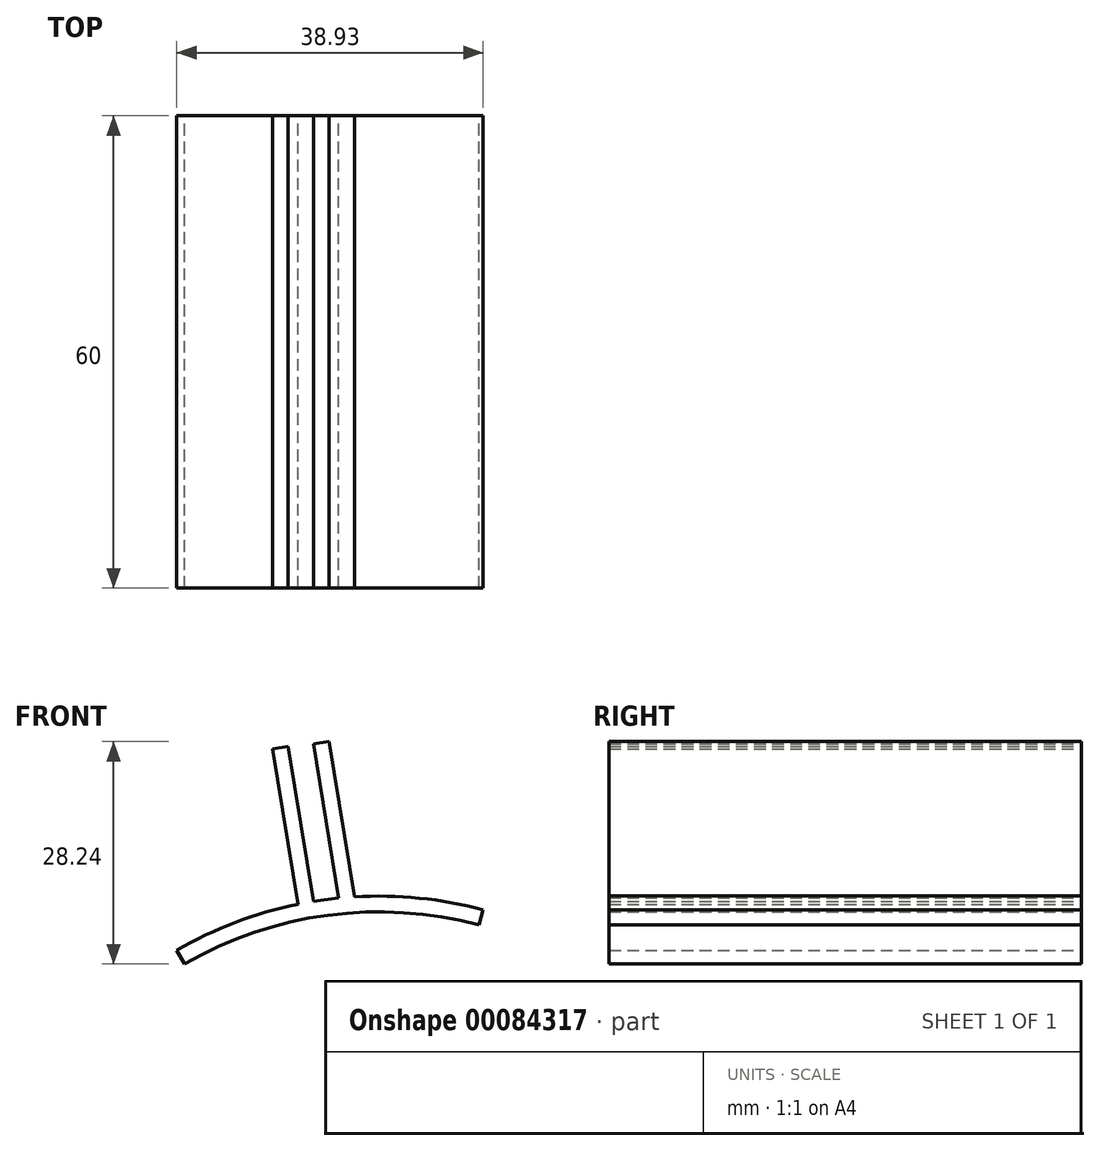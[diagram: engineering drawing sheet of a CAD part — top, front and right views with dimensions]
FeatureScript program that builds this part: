
annotation { "Feature Type Name" : "Feature", "Feature Type Description" : "" }
export const myFeature = defineFeature(function(context is Context, id is Id, definition is map)
    precondition{}
    {
        {
            var Q0;
            Q0=qCreatedBy(makeId("Front.planeOp"),FACE);
            var sketch = newSketch(context, id + "F0", { "sketchPlane" : qUnion([Q0])});
            skCircle(sketch, "E0", {"center": v(0, 0) * mm, "radius": 49.3 * mm});
            skLineSegment(sketch, "E1", {"start": v(0, 0) * mm, "end": v(-24.65, 42.7) * mm});
            skLineSegment(sketch, "E2", {"start": v(0, 0) * mm, "end": v(49.3, 0) * mm});
            skLineSegment(sketch, "E3", {"start": v(0, 0) * mm, "end": v(-24.65, -42.7) * mm});
            skArc(sketch, "E4", {"start": v(-24.65, 42.7) * mm, "mid": v(-6.43, 48.88) * mm, "end": v(12.76, 47.62) * mm});
            skLineSegment(sketch, "E5", {"start": v(0, 0) * mm, "end": v(12.76, 47.62) * mm});
            skArc(sketch, "E6", {"start": v(-24.65, -42.7) * mm, "mid": v(-14.82, -47.02) * mm, "end": v(-4.3, -49.11) * mm});
            skLineSegment(sketch, "E7", {"start": v(0, 0) * mm, "end": v(-4.3, -49.11) * mm});
            skArc(sketch, "E8", {"start": v(49.3, 0) * mm, "mid": v(48.13, 10.67) * mm, "end": v(44.68, 20.84) * mm});
            skLineSegment(sketch, "E9", {"start": v(0, 0) * mm, "end": v(44.68, 20.84) * mm});
            skCircle(sketch, "E10", {"center": v(0, 0) * mm, "radius": 51.3 * mm});
            skLineSegment(sketch, "E11", {"start": v(12.76, 47.62) * mm, "end": v(13.28, 49.55) * mm});
            skLineSegment(sketch, "E12", {"start": v(-24.65, 42.7) * mm, "end": v(-25.65, 44.43) * mm});
            skLineSegment(sketch, "E13", {"start": v(-24.65, -42.7) * mm, "end": v(-31.2, -40.72) * mm});
            skLineSegment(sketch, "E14", {"start": v(-8.3, 50.62) * mm, "end": v(-11.53, 70.32) * mm});
            skLineSegment(sketch, "E15", {"start": v(-5.09, 51.05) * mm, "end": v(-8.3, 70.62) * mm});
            skLineSegment(sketch, "E16", {"start": v(-8.3, 70.62) * mm, "end": v(-6.32, 70.94) * mm});
            skLineSegment(sketch, "E17", {"start": v(-6.32, 70.94) * mm, "end": v(-3.09, 51.2) * mm});
            skLineSegment(sketch, "E18", {"start": v(-11.53, 70.32) * mm, "end": v(-13.5, 70) * mm});
            skLineSegment(sketch, "E19", {"start": v(-13.5, 70) * mm, "end": v(-10.27, 50.26) * mm});
            skLineSegment(sketch, "E20", {"start": v(-11.53, 70.32) * mm, "end": v(-8.3, 70.62) * mm});
            skLineSegment(sketch, "E21", {"start": v(-8.3, 50.62) * mm, "end": v(-5.09, 51.05) * mm});
            skLineSegment(sketch, "E22", {"start": v(-6.7, 50.84) * mm, "end": v(0, 0) * mm});
            skSolve(sketch);
        }
        {
            var Q0;
            {var subQ2=sQuery(id+"F0.wireOp",EDGE,"E11");Q0=makeQuery(id+"F0.imprint","IMPRINT",FACE,{"disambiguationData":[TD([[makeQuery(id+"F0.imprint","IMPRINT",EDGE,{"derivedFrom":subQ2}),1.0]])]});}
            var Q1;
            {var subQ0=sQuery(id+"F0.wireOp",EDGE,"E14");Q1=makeQuery(id+"F0.imprint","IMPRINT",FACE,{"disambiguationData":[TD([[makeQuery(id+"F0.imprint","IMPRINT",EDGE,{"derivedFrom":subQ0}),1.0]])]});}
            var Q2;
            {var subQ0=sQuery(id+"F0.wireOp",EDGE,"E15");Q2=makeQuery(id+"F0.imprint","IMPRINT",FACE,{"disambiguationData":[TD([[makeQuery(id+"F0.imprint","IMPRINT",EDGE,{"derivedFrom":subQ0}),-1.0]])]});}
            var Q3;
            {var subQ0=sQuery(id+"F0.wireOp",EDGE,"E12");Q3=makeQuery(id+"F0.imprint","IMPRINT",FACE,{"disambiguationData":[TD([[makeQuery(id+"F0.imprint","IMPRINT",EDGE,{"derivedFrom":subQ0}),-1.0]])]});}
            extrude(context, id + "F1", {"entities" : qUnion([Q0, Q1, Q2, Q3]), "depth" : 60 * mm});
        }
    });
